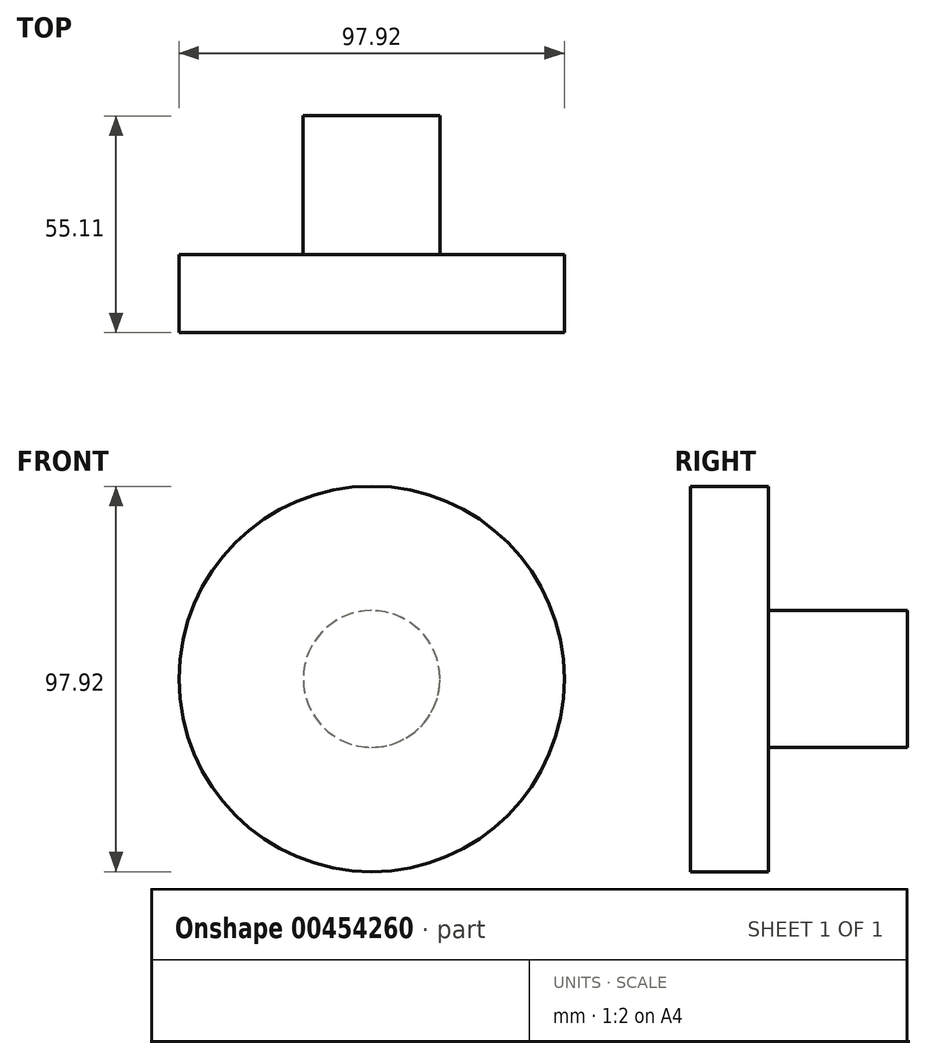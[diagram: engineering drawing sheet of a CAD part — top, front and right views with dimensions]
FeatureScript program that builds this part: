
annotation { "Feature Type Name" : "Feature", "Feature Type Description" : "" }
export const myFeature = defineFeature(function(context is Context, id is Id, definition is map)
    precondition{}
    {
        {
            var Q0;
            Q0=qCreatedBy(makeId("Top.planeOp"),FACE);
            var sketch = newSketch(context, id + "F0", { "sketchPlane" : qUnion([Q0])});
            skLineSegment(sketch, "E0.bottom", {"start": v(0, 0) * mm, "end": v(-48.96, 0) * mm});
            skLineSegment(sketch, "E0.top", {"start": v(0, 55.11) * mm, "end": v(-48.96, 55.11) * mm});
            skLineSegment(sketch, "E0.left", {"start": v(0, 0) * mm, "end": v(0, 55.11) * mm});
            skLineSegment(sketch, "E0.right", {"start": v(-48.96, 0) * mm, "end": v(-48.96, 55.11) * mm});
            skSolve(sketch);
        }
        {
            var Q0;
            Q0=makeQuery(id+"F0.imprint","IMPRINT",FACE,{"disambiguationData":[TD([[makeQuery(id+"F0.imprint","IMPRINT",EDGE,{"derivedFrom":sQuery(id+"F0.wireOp",EDGE,"E0.bottom")}),-1.0]])]});
            var Q1;
            Q1=sQuery(id+"F0.wireOp",EDGE,"E0.left");
            revolve(context, id + "F1", {"entities" : qUnion([Q0]), "axis" : qUnion([Q1]), "revolveType" : RevolveType.FULL});
        }
        {
            var Q0;
            Q0=qCreatedBy(makeId("Top.planeOp"),FACE);
            var sketch = newSketch(context, id + "F2", { "sketchPlane" : qUnion([Q0])});
            skLineSegment(sketch, "E1.bottom", {"start": v(-49.69, 55.35) * mm, "end": v(-17.37, 55.35) * mm});
            skLineSegment(sketch, "E1.top", {"start": v(-49.69, 19.9) * mm, "end": v(-17.37, 19.9) * mm});
            skLineSegment(sketch, "E1.left", {"start": v(-49.69, 55.35) * mm, "end": v(-49.69, 19.9) * mm});
            skLineSegment(sketch, "E1.right", {"start": v(-17.37, 55.35) * mm, "end": v(-17.37, 19.9) * mm});
            skLineSegment(sketch, "E2", {"start": v(0, 56.32) * mm, "end": v(0, 0) * mm});
            skSolve(sketch);
        }
        {
            var Q0;
            Q0 = qSketchRegion(id + "F2", true);
            var Q1;
            Q1=sQuery(id+"F2.wireOp",EDGE,"E2");
            revolve(context, id + "F3", {"operationType" : NewBodyOperationType.REMOVE, "entities" : qUnion([Q0]), "axis" : qUnion([Q1]), "revolveType" : RevolveType.FULL});
        }
    });
